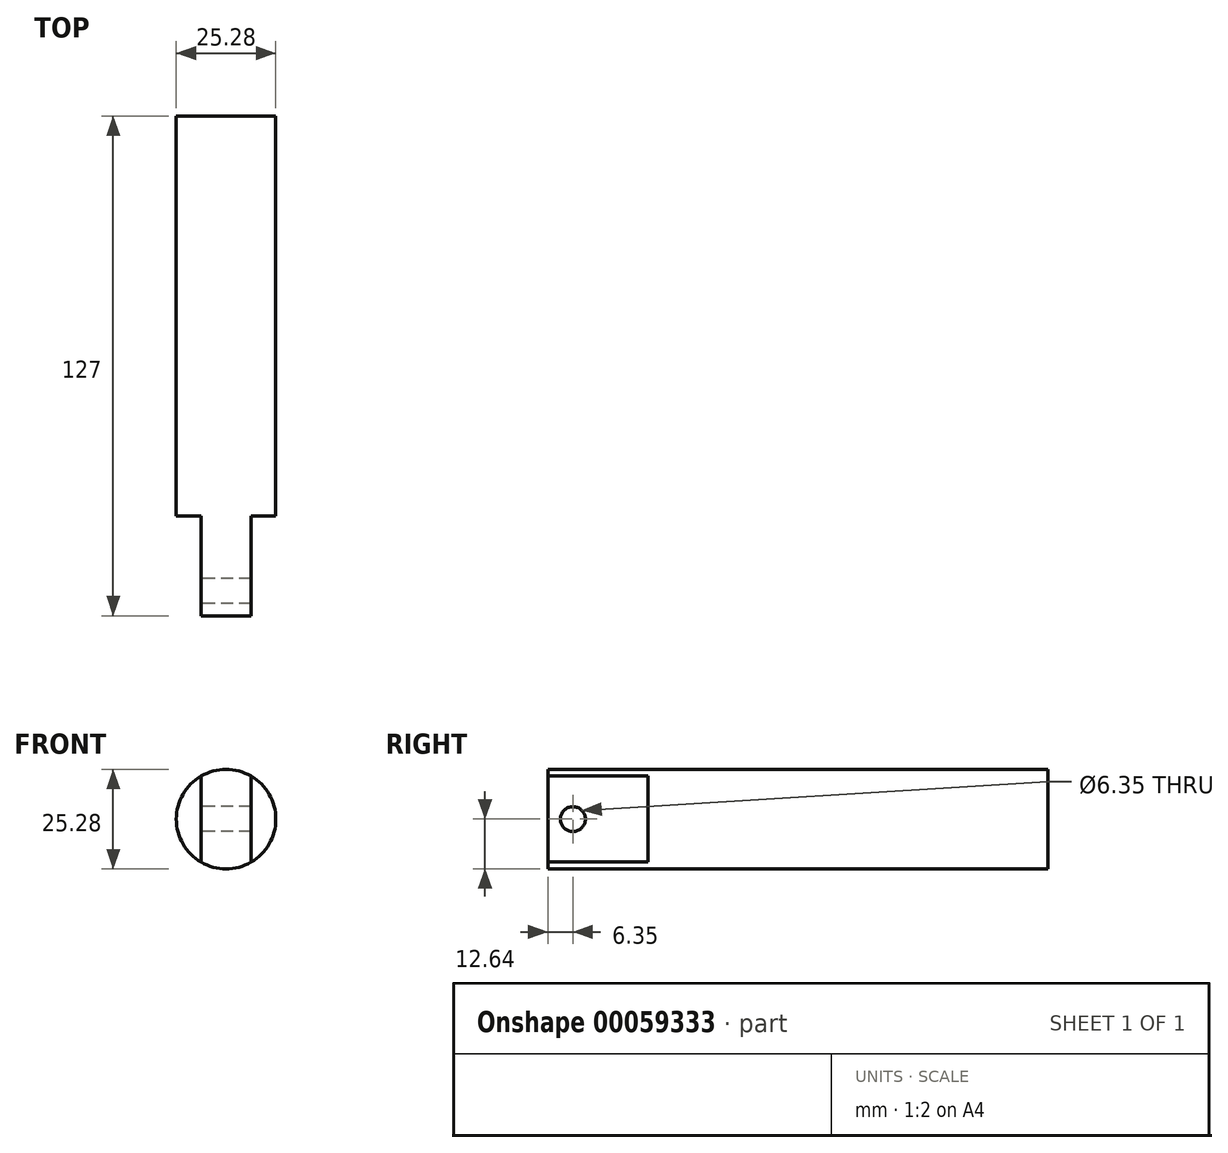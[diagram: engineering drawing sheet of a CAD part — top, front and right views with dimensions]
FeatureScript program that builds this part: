
annotation { "Feature Type Name" : "Feature", "Feature Type Description" : "" }
export const myFeature = defineFeature(function(context is Context, id is Id, definition is map)
    precondition{}
    {
        {
            var Q0;
            Q0=qCreatedBy(makeId("Front.planeOp"),FACE);
            var sketch = newSketch(context, id + "F0", { "sketchPlane" : qUnion([Q0])});
            skCircle(sketch, "E0", {"center": v(0, 0) * mm, "radius": 12.64 * mm});
            skSolve(sketch);
        }
        {
            var Q0;
            Q0 = qSketchRegion(id + "F0", true);
            extrude(context, id + "F1", {"entities" : qUnion([Q0]), "depth" : 127 * mm});
        }
        {
            var Q0;
            Q0=makeQuery(id+"F1.opExtrude","CAP_FACE",FACE,{"disambiguationData":[OSD([sQuery(id+"F0.wireOp",EDGE,"E0")])],"isStart":false});
            var sketch = newSketch(context, id + "F2", { "sketchPlane" : qUnion([Q0])});
            skLineSegment(sketch, "E1.bottom", {"start": v(-21.12, 19.96) * mm, "end": v(-6.35, 19.96) * mm});
            skLineSegment(sketch, "E1.top", {"start": v(-21.12, -23.59) * mm, "end": v(-6.35, -23.59) * mm});
            skLineSegment(sketch, "E1.left", {"start": v(-21.12, 19.96) * mm, "end": v(-21.12, -23.59) * mm});
            skLineSegment(sketch, "E1.right", {"start": v(-6.35, 19.96) * mm, "end": v(-6.35, -23.59) * mm});
            skLineSegment(sketch, "E2.bottom", {"start": v(6.35, 19.96) * mm, "end": v(21.9, 19.96) * mm});
            skLineSegment(sketch, "E2.top", {"start": v(6.35, -24.88) * mm, "end": v(21.9, -24.88) * mm});
            skLineSegment(sketch, "E2.left", {"start": v(6.35, 19.96) * mm, "end": v(6.35, -24.88) * mm});
            skLineSegment(sketch, "E2.right", {"start": v(21.9, 19.96) * mm, "end": v(21.9, -24.88) * mm});
            skSolve(sketch);
        }
        {
            var Q0;
            Q0 = qSketchRegion(id + "F2", true);
            extrude(context, id + "F3", {"entities" : qUnion([Q0]), "operationType" : NewBodyOperationType.REMOVE, "oppositeDirection" : true, "depth" : 25.4 * mm});
        }
        {
            var Q0;
            Q0=makeQuery(id+"F3.boolean.opBoolean","COPY",FACE,{"derivedFrom":makeQuery(id+"F3.opExtrude","SWEPT_FACE",FACE,{"disambiguationData":[OSD([sQuery(id+"F2.wireOp",EDGE,"E1.right")])]})});
            var sketch = newSketch(context, id + "F4", { "sketchPlane" : qUnion([Q0])});
            skCircle(sketch, "E3", {"center": v(120.65, 0) * mm, "radius": 3.18 * mm});
            skSolve(sketch);
        }
        {
            var Q0;
            Q0 = qSketchRegion(id + "F4", true);
            extrude(context, id + "F5", {"entities" : qUnion([Q0]), "operationType" : NewBodyOperationType.REMOVE, "oppositeDirection" : true, "depth" : 25.4 * mm});
        }
    });
